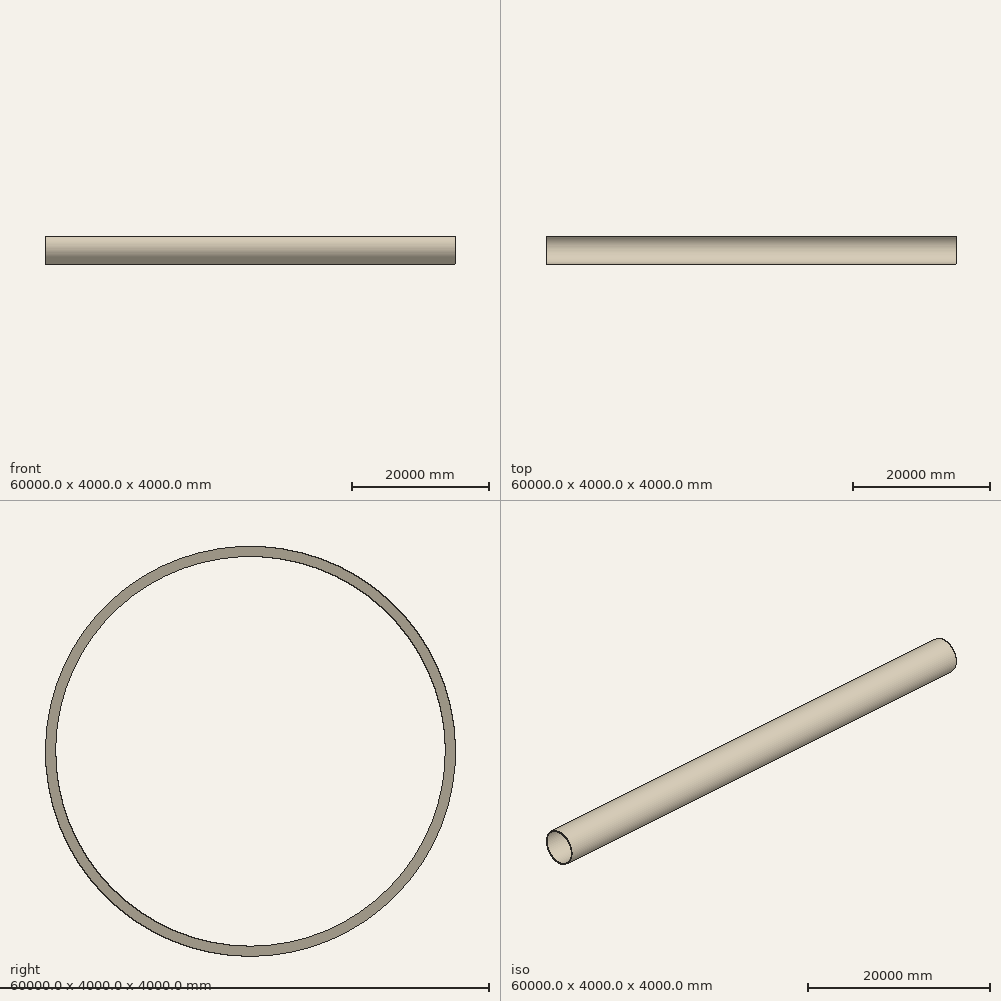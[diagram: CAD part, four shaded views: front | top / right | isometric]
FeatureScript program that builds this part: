
annotation { "Feature Type Name" : "Feature", "Feature Type Description" : "" }
export const myFeature = defineFeature(function(context is Context, id is Id, definition is map)
    precondition{}
    {
        {
            var Q0;
            Q0=qCreatedBy(makeId("Right.planeOp"),FACE);
            var sketch = newSketch(context, id + "F0", { "sketchPlane" : qUnion([Q0])});
            skCircle(sketch, "E0", {"center": v(0, 0) * mm, "radius": 2000 * mm});
            skSolve(sketch);
        }
        {
            var Q0;
            Q0=makeQuery(id+"F0.imprint","IMPRINT",FACE,{"disambiguationData":[TD([[makeQuery(id+"F0.imprint","IMPRINT",EDGE,{"derivedFrom":sQuery(id+"F0.wireOp",EDGE,"E0")}),1.0]])]});
            var Q1;
            Q1=sQuery(id+"F0.wireOp",EDGE,"E0");
            extrude(context, id + "F1", {"entities" : qUnion([Q0]), "flatOperationType" : FlatOperationType.REMOVE, "surfaceEntities" : qUnion([Q1]), "offsetDistance" : 25 * mm, "depth" : 60000 * mm, "domain" : OperationDomain.MODEL, "symmetric" : true});
        }
        {
            var Q0;
            Q0=makeQuery(id+"F1.opExtrude","CAP_FACE",FACE,{"disambiguationData":[OSD([sQuery(id+"F0.wireOp",EDGE,"E0")])],"isStart":false});
            var Q1;
            Q1=makeQuery(id+"F1.opExtrude","CAP_FACE",FACE,{"disambiguationData":[OSD([sQuery(id+"F0.wireOp",EDGE,"E0")])],"isStart":true});
            shell(context, id + "F2", {"entities" : qUnion([Q0, Q1]), "thickness" : 100 * mm});
        }
    });
